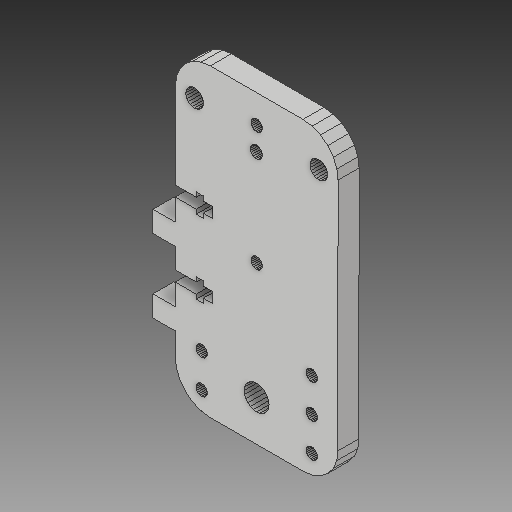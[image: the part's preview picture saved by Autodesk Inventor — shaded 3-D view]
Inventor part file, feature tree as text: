
AUTODESK INVENTOR PART (.ipt)
format: ipt  version: 2017 (Build 210142000, 142)  size: 583,680 bytes
history: native  units: mm
features: other x3, sketch x1
ambient origin geometry x8: Origin, YZ Plane, XZ Plane, XY Plane, X Axis, Y Axis, Z Axis, Center Point
bodies: Solid1 (feature_tree)
feature tree (4):
  other  "Hotend Rear Plate_MIR.ipt"
  other  "Solid1::Hotend Rear Plate_MIR.ipt"
  other  "TaggingFeature1"
  sketch  "Sketch1"  dims[d0=10.0mm]
